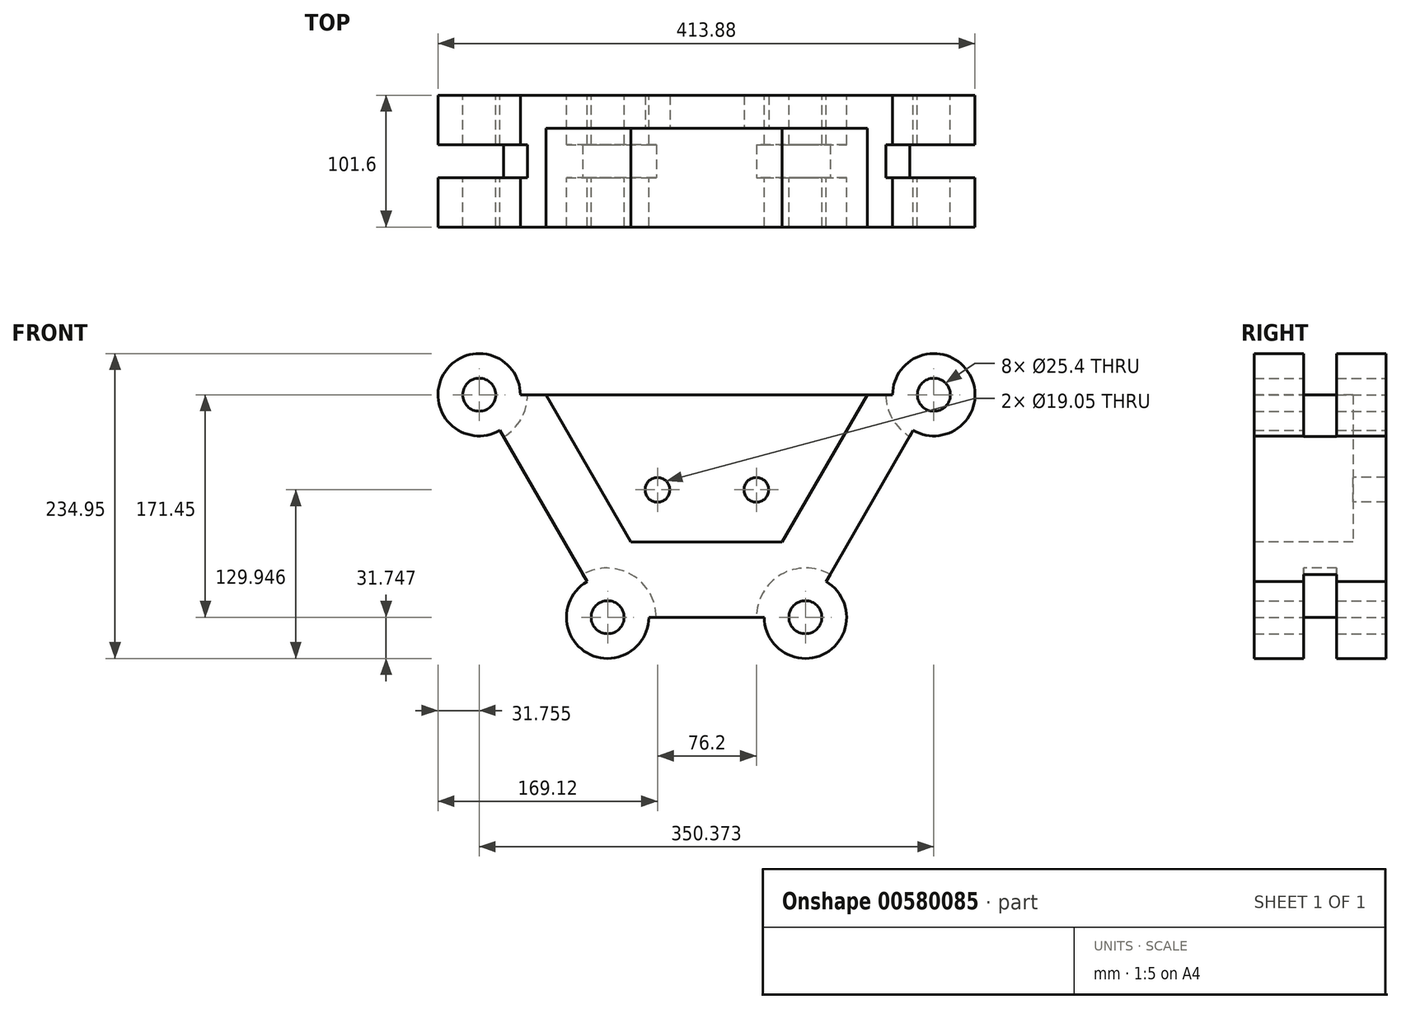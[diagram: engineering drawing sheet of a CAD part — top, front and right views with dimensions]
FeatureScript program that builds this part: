
annotation { "Feature Type Name" : "Feature", "Feature Type Description" : "" }
export const myFeature = defineFeature(function(context is Context, id is Id, definition is map)
    precondition{}
    {
        {
            var Q0;
            Q0=qCreatedBy(makeId("Front.planeOp"),FACE);
            var sketch = newSketch(context, id + "F0", { "sketchPlane" : qUnion([Q0])});
            skLineSegment(sketch, "E0", {"start": v(-76.48, -86.88) * mm, "end": v(75.92, -86.88) * mm});
            skLineSegment(sketch, "E1", {"start": v(75.92, -86.88) * mm, "end": v(174.9, 84.57) * mm});
            skLineSegment(sketch, "E2", {"start": v(174.9, 84.57) * mm, "end": v(-175.47, 84.57) * mm});
            skLineSegment(sketch, "E3", {"start": v(-175.47, 84.57) * mm, "end": v(-76.48, -86.88) * mm});
            skCircle(sketch, "E4", {"center": v(-175.47, 84.57) * mm, "radius": 12.7 * mm});
            skCircle(sketch, "E5", {"center": v(-175.47, 84.57) * mm, "radius": 31.75 * mm});
            skCircle(sketch, "E6", {"center": v(174.9, 84.57) * mm, "radius": 12.7 * mm});
            skCircle(sketch, "E7", {"center": v(174.9, 84.57) * mm, "radius": 31.75 * mm});
            skCircle(sketch, "E8", {"center": v(-76.48, -86.88) * mm, "radius": 12.7 * mm});
            skCircle(sketch, "E9", {"center": v(75.92, -86.88) * mm, "radius": 12.7 * mm});
            skCircle(sketch, "E10", {"center": v(-76.48, -86.88) * mm, "radius": 31.75 * mm});
            skCircle(sketch, "E11", {"center": v(75.92, -86.88) * mm, "radius": 31.75 * mm});
            skSolve(sketch);
        }
        {
            var Q0;
            {var subQ3=sQuery(id+"F0.wireOp",EDGE,"E10");var subQ10=sQuery(id+"F0.wireOp",EDGE,"E0");var subQ15=makeQuery(id+"F0.imprint","INTERSECT",VERTEX,{"derivedFrom":[subQ10,subQ3]});Q0=makeQuery(id+"F0.imprint","IMPRINT",FACE,{"disambiguationData":[TD([[makeQuery(id+"F0.imprint","IMPRINT",EDGE,{"disambiguationData":[TD([[subQ15,-1.0]])],"derivedFrom":subQ10}),1.0]])]});}
            var Q1;
            {var subQ0=sQuery(id+"F0.wireOp",EDGE,"E5");var subQ1=sQuery(id+"F0.wireOp",EDGE,"E2");var subQ2=makeQuery(id+"F0.imprint","INTERSECT",VERTEX,{"derivedFrom":[subQ1,subQ0]});Q1=makeQuery(id+"F0.imprint","IMPRINT",FACE,{"disambiguationData":[TD([[makeQuery(id+"F0.imprint","IMPRINT",EDGE,{"disambiguationData":[TD([[subQ2,-1.0]])],"derivedFrom":subQ1}),-1.0]])]});}
            var Q2;
            {var subQ0=sQuery(id+"F0.wireOp",EDGE,"E5");var subQ1=sQuery(id+"F0.wireOp",EDGE,"E2");var subQ2=makeQuery(id+"F0.imprint","INTERSECT",VERTEX,{"derivedFrom":[subQ1,subQ0]});Q2=makeQuery(id+"F0.imprint","IMPRINT",FACE,{"disambiguationData":[TD([[makeQuery(id+"F0.imprint","IMPRINT",EDGE,{"disambiguationData":[TD([[subQ2,-1.0]])],"derivedFrom":subQ1}),1.0]])]});}
            var Q3;
            {var subQ0=sQuery(id+"F0.wireOp",EDGE,"E7");var subQ1=sQuery(id+"F0.wireOp",EDGE,"E1");var subQ2=makeQuery(id+"F0.imprint","INTERSECT",VERTEX,{"derivedFrom":[subQ1,subQ0]});Q3=makeQuery(id+"F0.imprint","IMPRINT",FACE,{"disambiguationData":[TD([[makeQuery(id+"F0.imprint","IMPRINT",EDGE,{"disambiguationData":[TD([[subQ2,-1.0]])],"derivedFrom":subQ1}),1.0]])]});}
            var Q4;
            {var subQ0=sQuery(id+"F0.wireOp",EDGE,"E7");var subQ1=sQuery(id+"F0.wireOp",EDGE,"E1");var subQ2=makeQuery(id+"F0.imprint","INTERSECT",VERTEX,{"derivedFrom":[subQ1,subQ0]});Q4=makeQuery(id+"F0.imprint","IMPRINT",FACE,{"disambiguationData":[TD([[makeQuery(id+"F0.imprint","IMPRINT",EDGE,{"disambiguationData":[TD([[subQ2,-1.0]])],"derivedFrom":subQ1}),-1.0]])]});}
            var Q5;
            {var subQ0=sQuery(id+"F0.wireOp",EDGE,"E11");var subQ1=sQuery(id+"F0.wireOp",EDGE,"E0");var subQ2=makeQuery(id+"F0.imprint","INTERSECT",VERTEX,{"derivedFrom":[subQ1,subQ0]});Q5=makeQuery(id+"F0.imprint","IMPRINT",FACE,{"disambiguationData":[TD([[makeQuery(id+"F0.imprint","IMPRINT",EDGE,{"disambiguationData":[TD([[subQ2,-1.0]])],"derivedFrom":subQ1}),1.0]])]});}
            var Q6;
            {var subQ0=sQuery(id+"F0.wireOp",EDGE,"E11");var subQ1=sQuery(id+"F0.wireOp",EDGE,"E0");var subQ2=makeQuery(id+"F0.imprint","INTERSECT",VERTEX,{"derivedFrom":[subQ1,subQ0]});Q6=makeQuery(id+"F0.imprint","IMPRINT",FACE,{"disambiguationData":[TD([[makeQuery(id+"F0.imprint","IMPRINT",EDGE,{"disambiguationData":[TD([[subQ2,-1.0]])],"derivedFrom":subQ1}),-1.0]])]});}
            var Q7;
            {var subQ0=sQuery(id+"F0.wireOp",EDGE,"E10");var subQ1=sQuery(id+"F0.wireOp",EDGE,"E0");var subQ2=makeQuery(id+"F0.imprint","INTERSECT",VERTEX,{"derivedFrom":[subQ1,subQ0]});Q7=makeQuery(id+"F0.imprint","IMPRINT",FACE,{"disambiguationData":[TD([[makeQuery(id+"F0.imprint","IMPRINT",EDGE,{"disambiguationData":[TD([[subQ2,1.0]])],"derivedFrom":subQ1}),1.0]])]});}
            var Q8;
            {var subQ0=sQuery(id+"F0.wireOp",EDGE,"E10");var subQ1=sQuery(id+"F0.wireOp",EDGE,"E0");var subQ2=makeQuery(id+"F0.imprint","INTERSECT",VERTEX,{"derivedFrom":[subQ1,subQ0]});Q8=makeQuery(id+"F0.imprint","IMPRINT",FACE,{"disambiguationData":[TD([[makeQuery(id+"F0.imprint","IMPRINT",EDGE,{"disambiguationData":[TD([[subQ2,1.0]])],"derivedFrom":subQ1}),-1.0]])]});}
            var Q9;
            Q9=sQuery(id+"F0.wireOp",EDGE,"E11");
            var Q10;
            Q10=sQuery(id+"F0.wireOp",EDGE,"E10");
            var Q11;
            Q11=sQuery(id+"F0.wireOp",EDGE,"E5");
            var Q12;
            Q12=sQuery(id+"F0.wireOp",EDGE,"E7");
            var Q13;
            Q13=sQuery(id+"F0.wireOp",EDGE,"E0");
            var Q14;
            Q14=sQuery(id+"F0.wireOp",EDGE,"E3");
            var Q15;
            Q15=sQuery(id+"F0.wireOp",EDGE,"E2");
            var Q16;
            Q16=sQuery(id+"F0.wireOp",EDGE,"E1");
            var Q17;
            Q17=sQuery(id+"F0.wireOp",EDGE,"E9");
            var Q18;
            Q18=sQuery(id+"F0.wireOp",EDGE,"E8");
            var Q19;
            Q19=sQuery(id+"F0.wireOp",EDGE,"E6");
            var Q20;
            Q20=sQuery(id+"F0.wireOp",EDGE,"E4");
            extrude(context, id + "F1", {"entities" : qUnion([Q0, Q1, Q2, Q3, Q4, Q5, Q6, Q7, Q8]), "surfaceEntities" : qUnion([Q9, Q10, Q11, Q12, Q13, Q14, Q15, Q16, Q17, Q18, Q19, Q20]), "endBound" : BoundingType.SYMMETRIC, "depth" : 101.6 * mm, "offsetDistance" : 25.4 * mm});
        }
        {
            var Q0;
            Q0=makeQuery(id+"F1.opExtrude","CAP_FACE",FACE,{"disambiguationData":[OSD([sQuery(id+"F0.wireOp",EDGE,"E0"),sQuery(id+"F0.wireOp",EDGE,"E1"),sQuery(id+"F0.wireOp",EDGE,"E2"),sQuery(id+"F0.wireOp",EDGE,"E3"),sQuery(id+"F0.wireOp",EDGE,"E4"),sQuery(id+"F0.wireOp",EDGE,"E5"),sQuery(id+"F0.wireOp",EDGE,"E6"),sQuery(id+"F0.wireOp",EDGE,"E7"),sQuery(id+"F0.wireOp",EDGE,"E8"),sQuery(id+"F0.wireOp",EDGE,"E9"),sQuery(id+"F0.wireOp",EDGE,"E10"),sQuery(id+"F0.wireOp",EDGE,"E11")])],"isStart":false});
            var sketch = newSketch(context, id + "F2", { "sketchPlane" : qUnion([Q0])});
            skLineSegment(sketch, "E12", {"start": v(-124.14, 84.57) * mm, "end": v(123.58, 84.57) * mm});
            skLineSegment(sketch, "E13", {"start": v(123.58, 84.57) * mm, "end": v(58.07, -28.9) * mm});
            skLineSegment(sketch, "E14", {"start": v(58.07, -28.9) * mm, "end": v(-58.63, -28.9) * mm});
            skLineSegment(sketch, "E15", {"start": v(-58.63, -28.9) * mm, "end": v(-124.14, 84.57) * mm});
            skSolve(sketch);
        }
        {
            var Q0;
            Q0=makeQuery(id+"F2.imprint","IMPRINT",FACE,{"disambiguationData":[TD([[makeQuery(id+"F2.imprint","IMPRINT",EDGE,{"derivedFrom":sQuery(id+"F2.wireOp",EDGE,"E12")}),1.0]])]});
            extrude(context, id + "F3", {"entities" : qUnion([Q0]), "operationType" : NewBodyOperationType.REMOVE, "oppositeDirection" : true, "depth" : 76.2 * mm, "offsetDistance" : 25.4 * mm});
        }
        {
            var Q0;
            Q0=qCreatedBy(makeId("Front.planeOp"),FACE);
            var sketch = newSketch(context, id + "F4", { "sketchPlane" : qUnion([Q0])});
            skCircle(sketch, "E16", {"center": v(-176.31, 84.72) * mm, "radius": 38.1 * mm});
            skCircle(sketch, "E17", {"center": v(176.03, 85.03) * mm, "radius": 38.1 * mm});
            skCircle(sketch, "E18", {"center": v(76.21, -87.07) * mm, "radius": 38.1 * mm});
            skCircle(sketch, "E19", {"center": v(-77.12, -87.07) * mm, "radius": 38.1 * mm});
            skSolve(sketch);
        }
        {
            var Q0;
            Q0=makeQuery(id+"F4.imprint","IMPRINT",FACE,{"disambiguationData":[TD([[makeQuery(id+"F4.imprint","IMPRINT",EDGE,{"derivedFrom":sQuery(id+"F4.wireOp",EDGE,"E16")}),1.0]])]});
            var Q1;
            Q1=makeQuery(id+"F4.imprint","IMPRINT",FACE,{"disambiguationData":[TD([[makeQuery(id+"F4.imprint","IMPRINT",EDGE,{"derivedFrom":sQuery(id+"F4.wireOp",EDGE,"E17")}),1.0]])]});
            var Q2;
            Q2=makeQuery(id+"F4.imprint","IMPRINT",FACE,{"disambiguationData":[TD([[makeQuery(id+"F4.imprint","IMPRINT",EDGE,{"derivedFrom":sQuery(id+"F4.wireOp",EDGE,"E18")}),1.0]])]});
            var Q3;
            Q3=makeQuery(id+"F4.imprint","IMPRINT",FACE,{"disambiguationData":[TD([[makeQuery(id+"F4.imprint","IMPRINT",EDGE,{"derivedFrom":sQuery(id+"F4.wireOp",EDGE,"E19")}),1.0]])]});
            extrude(context, id + "F5", {"entities" : qUnion([Q0, Q1, Q2, Q3]), "operationType" : NewBodyOperationType.REMOVE, "endBound" : BoundingType.SYMMETRIC, "oppositeDirection" : true, "depth" : 25.4 * mm, "offsetDistance" : 25.4 * mm});
        }
        {
            var Q0;
            {var subQ3=sQuery(id+"F0.wireOp",EDGE,"E10");var subQ10=sQuery(id+"F0.wireOp",EDGE,"E0");var subQ15=makeQuery(id+"F0.imprint","INTERSECT",VERTEX,{"derivedFrom":[subQ10,subQ3]});Q0=makeQuery(id+"F0.imprint","IMPRINT",FACE,{"disambiguationData":[TD([[makeQuery(id+"F0.imprint","IMPRINT",EDGE,{"disambiguationData":[TD([[subQ15,-1.0]])],"derivedFrom":subQ10}),1.0]])]});}
            var sketch = newSketch(context, id + "F6", { "sketchPlane" : qUnion([Q0])});
            skLineSegment(sketch, "E20", {"start": v(38.1, -48.78) * mm, "end": v(-38.1, -48.78) * mm, "construction": true});
            skCircle(sketch, "E21", {"center": v(38.1, -48.78) * mm, "radius": 9.53 * mm});
            skCircle(sketch, "E22", {"center": v(-38.1, -48.78) * mm, "radius": 9.53 * mm});
            skLineSegment(sketch, "E23", {"start": v(0, 0) * mm, "end": v(0, -74.8) * mm, "construction": true});
            skSolve(sketch);
        }
        {
            var Q0;
            Q0=makeQuery(id+"F6.imprint","IMPRINT",FACE,{"disambiguationData":[TD([[makeQuery(id+"F6.imprint","IMPRINT",EDGE,{"derivedFrom":sQuery(id+"F6.wireOp",EDGE,"E21")}),-1.0]])]});
            var sketch = newSketch(context, id + "F7", { "sketchPlane" : qUnion([Q0])});
            skLineSegment(sketch, "E24", {"start": v(0, -26.78) * mm, "end": v(0, 11.32) * mm, "construction": true});
            skLineSegment(sketch, "E25", {"start": v(-38.1, 11.32) * mm, "end": v(38.1, 11.32) * mm, "construction": true});
            skCircle(sketch, "E26", {"center": v(-38.1, 11.32) * mm, "radius": 9.53 * mm});
            skCircle(sketch, "E27", {"center": v(38.1, 11.32) * mm, "radius": 9.53 * mm});
            skSolve(sketch);
        }
        {
            var Q0;
            Q0 = qSketchRegion(id + "F7", true);
            extrude(context, id + "F8", {"entities" : qUnion([Q0]), "operationType" : NewBodyOperationType.REMOVE, "endBound" : BoundingType.THROUGH_ALL, "oppositeDirection" : true, "depth" : 25.4 * mm, "offsetDistance" : 25.4 * mm});
        }
    });
